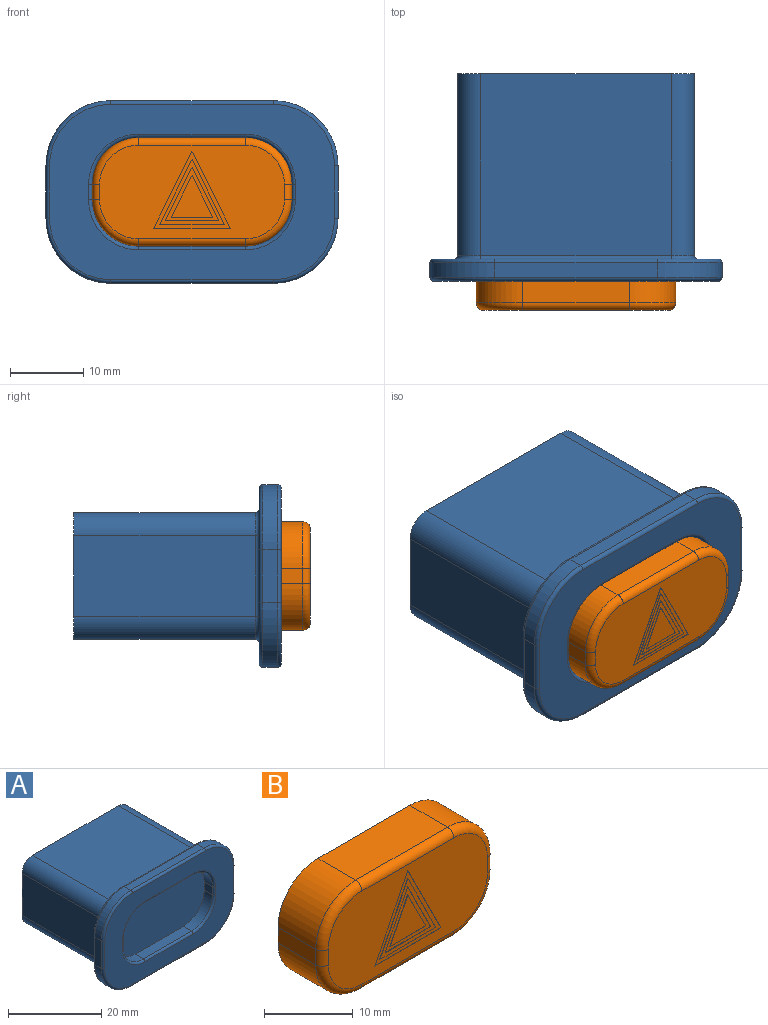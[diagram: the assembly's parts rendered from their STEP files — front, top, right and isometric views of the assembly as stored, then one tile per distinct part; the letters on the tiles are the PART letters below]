
ASSEMBLY  parts=2 mates=1
PART A: 60 faces, bbox 41.5x28.4x26.5 mm
  f0: plane 22.22x2mm, normal (0,0,1), area 44.4mm2, adj f1,f7,f47,f55
  f1: cylinder r=8.89mm len=8.89mm, axis (0,1,0), area 27.9mm2, adj f0,f2,f45,f53
  f2: plane 7.22x2mm, normal (-1,0,0), area 14.4mm2, adj f1,f3,f44,f52
  f3: cylinder r=8.89mm len=8.89mm, axis (0,1,0), area 27.9mm2, adj f2,f4,f46,f54
  f4: plane 22.22x2mm, normal (0,0,-1), area 44.4mm2, adj f3,f5,f48,f56
  f5: cylinder r=8.89mm len=8.89mm, axis (0,1,0), area 27.9mm2, adj f4,f6,f50,f58
  f6: plane 7.22x2mm, normal (1,0,0), area 14.4mm2, adj f5,f7,f51,f59
  f7: cylinder r=8.89mm len=8.89mm, axis (0,1,0), area 27.9mm2, adj f0,f6,f49,f57
  f8: plane 39x24mm, normal (0,-1,0), area 467.6mm2, adj f28,f29,f30,f31,f32,f33,f34,f35
  f9: plane 39x24mm, normal (0,1,0), area 273.6mm2, adj f36,f37,f38,f39,f40,f41,f42,f43
  f10: plane 24.9x11.03mm, normal (1,0,0), area 274.6mm2, adj f11,f17,f18,f40
  f11: cylinder r=3.17mm len=24.9mm, axis (0,-1,0), area 124.2mm2, adj f10,f12,f18,f38
  f12: plane 26.03x24.9mm, normal (0,0,-1), area 648.1mm2, adj f11,f13,f18,f36
  f13: cylinder r=3.17mm len=24.9mm, axis (0,-1,0), area 124.2mm2, adj f12,f14,f18,f37
  f14: plane 24.9x11.03mm, normal (-1,0,0), area 274.6mm2, adj f13,f15,f18,f39
  f15: cylinder r=3.17mm len=24.9mm, axis (0,-1,0), area 124.2mm2, adj f14,f16,f18,f41
  f16: plane 26.03x24.9mm, normal (0,0,1), area 648.1mm2, adj f15,f17,f18,f43
  f17: cylinder r=3.17mm len=24.9mm, axis (0,-1,0), area 124.2mm2, adj f10,f16,f18,f42
  f18: plane 32.38x17.38mm, normal (0,1,0), area 554.1mm2, adj f10,f11,f12,f13,f14,f15,f16,f17
  f19: plane 2.5x2.14mm, normal (1,0,0), area 5.4mm2, adj f20,f26,f27,f32
  f20: cylinder r=6.35mm len=6.35mm, axis (0,-1,0), area 24.9mm2, adj f19,f21,f27,f30
  f21: plane 14.6x2.5mm, normal (0,0,1), area 36.5mm2, adj f20,f22,f27,f28
  f22: cylinder r=6.35mm len=6.35mm, axis (0,-1,0), area 24.9mm2, adj f21,f23,f27,f29
  f23: plane 2.5x2.14mm, normal (-1,0,0), area 5.4mm2, adj f22,f24,f27,f31
  f24: cylinder r=6.35mm len=6.35mm, axis (0,-1,0), area 24.9mm2, adj f23,f25,f27,f33
  f25: plane 14.6x2.5mm, normal (0,0,-1), area 36.5mm2, adj f24,f26,f27,f35
  f26: cylinder r=6.35mm len=6.35mm, axis (0,-1,0), area 24.9mm2, adj f19,f25,f27,f34
  f27: plane 27.3x14.84mm, normal (0,-1,0), area 370.5mm2, adj f19,f20,f21,f22,f23,f24,f25,f26
  f28: cylinder r=0.5mm len=14.6mm, axis (-1,0,0), area 11.5mm2, adj f8,f21,f29,f30
  f29: torus R=6.85mm, axis (0,-1,0), area 8.1mm2, adj f8,f22,f28,f31
  f30: torus R=6.85mm, axis (0,-1,0), area 8.1mm2, adj f8,f20,f28,f32
  f31: cylinder r=0.5mm len=2.14mm, axis (0,0,-1), area 1.7mm2, adj f8,f23,f29,f33
  f32: cylinder r=0.5mm len=2.14mm, axis (0,0,1), area 1.7mm2, adj f8,f19,f30,f34
  f33: torus R=6.85mm, axis (0,-1,0), area 8.1mm2, adj f8,f24,f31,f35
  f34: torus R=6.85mm, axis (0,-1,0), area 8.1mm2, adj f8,f26,f32,f35
  f35: cylinder r=0.5mm len=14.6mm, axis (1,0,0), area 11.5mm2, adj f8,f25,f33,f34
  f36: cylinder r=0.5mm len=26.03mm, axis (1,0,0), area 20.4mm2, adj f9,f12,f37,f38
  f37: torus R=3.67mm, axis (0,-1,0), area 4.1mm2, adj f9,f13,f36,f39
  f38: torus R=3.67mm, axis (0,-1,0), area 4.1mm2, adj f9,f11,f36,f40
  f39: cylinder r=0.5mm len=11.03mm, axis (0,0,-1), area 8.7mm2, adj f9,f14,f37,f41
  f40: cylinder r=0.5mm len=11.03mm, axis (0,0,1), area 8.7mm2, adj f9,f10,f38,f42
  f41: torus R=3.67mm, axis (0,-1,0), area 4.1mm2, adj f9,f15,f39,f43
  f42: torus R=3.67mm, axis (0,-1,0), area 4.1mm2, adj f9,f17,f40,f43
  f43: cylinder r=0.5mm len=26.03mm, axis (-1,0,0), area 20.4mm2, adj f9,f16,f41,f42
  f44: cylinder r=0.5mm len=7.22mm, axis (0,0,-1), area 5.7mm2, adj f2,f9,f45,f46
  f45: torus R=8.39mm, axis (0,-1,0), area 10.7mm2, adj f1,f9,f44,f47
  f46: torus R=8.39mm, axis (0,-1,0), area 10.7mm2, adj f3,f9,f44,f48
  f47: cylinder r=0.5mm len=22.22mm, axis (-1,0,0), area 17.5mm2, adj f0,f9,f45,f49
  f48: cylinder r=0.5mm len=22.22mm, axis (1,0,0), area 17.5mm2, adj f4,f9,f46,f50
  f49: torus R=8.39mm, axis (0,-1,0), area 10.7mm2, adj f7,f9,f47,f51
  f50: torus R=8.39mm, axis (0,-1,0), area 10.7mm2, adj f5,f9,f48,f51
  f51: cylinder r=0.5mm len=7.22mm, axis (0,0,1), area 5.7mm2, adj f6,f9,f49,f50
  f52: cylinder r=0.5mm len=7.22mm, axis (0,0,1), area 5.7mm2, adj f2,f8,f53,f54
  f53: torus R=8.39mm, axis (0,-1,0), area 10.7mm2, adj f1,f8,f52,f55
  f54: torus R=8.39mm, axis (0,-1,0), area 10.7mm2, adj f3,f8,f52,f56
  f55: cylinder r=0.5mm len=22.22mm, axis (1,0,0), area 17.5mm2, adj f0,f8,f53,f57
  f56: cylinder r=0.5mm len=22.22mm, axis (-1,0,0), area 17.5mm2, adj f4,f8,f54,f58
  f57: torus R=8.39mm, axis (0,-1,0), area 10.7mm2, adj f7,f8,f55,f59
  f58: torus R=8.39mm, axis (0,-1,0), area 10.7mm2, adj f5,f8,f56,f59
  f59: cylinder r=0.5mm len=7.22mm, axis (0,0,-1), area 5.7mm2, adj f6,f8,f57,f58
PART B: 34 faces, bbox 28.3x7x15.9 mm
  f0: plane 25.3x12.84mm, normal (0,-1,0), area 245.1mm2, adj f10,f11,f12,f13,f14,f15,f16,f17
  f1: plane 6x2.14mm, normal (-1,0,0), area 12.8mm2, adj f2,f8,f9,f14
  f2: cylinder r=6.35mm len=6.35mm, axis (0,1,0), area 59.8mm2, adj f1,f3,f9,f12
  f3: plane 14.6x6mm, normal (0,0,-1), area 87.6mm2, adj f2,f4,f9,f10
  f4: cylinder r=6.35mm len=6.35mm, axis (0,1,0), area 59.8mm2, adj f3,f5,f9,f11
  f5: plane 6x2.14mm, normal (1,0,0), area 12.8mm2, adj f4,f6,f9,f13
  f6: cylinder r=6.35mm len=6.35mm, axis (0,1,0), area 59.8mm2, adj f5,f7,f9,f15
  f7: plane 14.6x6mm, normal (0,0,1), area 87.6mm2, adj f6,f8,f9,f17
  f8: cylinder r=6.35mm len=6.35mm, axis (0,1,0), area 59.8mm2, adj f1,f7,f9,f16
  f9: plane 27.3x14.84mm, normal (0,1,0), area 370.5mm2, adj f1,f2,f3,f4,f5,f6,f7,f8
  f10: cylinder r=1mm len=14.6mm, axis (-1,0,0), area 22.9mm2, adj f0,f3,f11,f12
  f11: torus R=5.35mm, axis (0,-1,0), area 14.8mm2, adj f0,f4,f10,f13
  f12: torus R=5.35mm, axis (0,-1,0), area 14.8mm2, adj f0,f2,f10,f14
  f13: cylinder r=1mm len=2.14mm, axis (0,0,-1), area 3.4mm2, adj f0,f5,f11,f15
  f14: cylinder r=1mm len=2.14mm, axis (0,0,1), area 3.4mm2, adj f0,f1,f12,f16
  f15: torus R=5.35mm, axis (0,-1,0), area 14.8mm2, adj f0,f6,f13,f17
  f16: torus R=5.35mm, axis (0,-1,0), area 14.8mm2, adj f0,f8,f14,f17
  f17: cylinder r=1mm len=14.6mm, axis (1,0,0), area 22.9mm2, adj f0,f7,f15,f16
  f18: plane 10.51x5.25mm, normal (0.89,0,-0.45), area 0.6mm2, adj f0,f19,f23,f24
  f19: plane 10.51x0.05mm, normal (0,0,1), area 0.5mm2, adj f0,f18,f23,f24
  f20: plane 8.89x0.05mm, normal (0,0,-1), area 0.4mm2, adj f21,f22,f24,f25
  f21: plane 8.89x4.45mm, normal (-0.89,0,0.45), area 0.5mm2, adj f20,f22,f24,f25
  f22: plane 8.89x4.45mm, normal (0.89,0,0.45), area 0.5mm2, adj f20,f21,f24,f25
  f23: plane 10.51x5.25mm, normal (-0.89,0,-0.45), area 0.6mm2, adj f0,f18,f19,f24
  f24: plane 10.51x10.51mm, normal (0,-1,0), area 15.7mm2, adj f18,f19,f20,f21,f22,f23
  f25: plane 8.89x8.89mm, normal (0,-1,0), area 13.1mm2, adj f20,f21,f22,f28,f29,f30
  f26: plane 5.65x2.83mm, normal (-0.89,0,0.45), area 0.3mm2, adj f27,f31,f32,f33
  f27: plane 5.65x2.83mm, normal (0.89,0,0.45), area 0.3mm2, adj f26,f31,f32,f33
  f28: plane 7.27x3.64mm, normal (-0.89,0,-0.45), area 0.4mm2, adj f25,f29,f30,f32
  f29: plane 7.27x3.64mm, normal (0.89,0,-0.45), area 0.4mm2, adj f25,f28,f30,f32
  f30: plane 7.27x0.05mm, normal (0,0,1), area 0.4mm2, adj f25,f28,f29,f32
  f31: plane 5.65x0.05mm, normal (0,0,-1), area 0.3mm2, adj f26,f27,f32,f33
  f32: plane 7.27x7.27mm, normal (0,-1,0), area 10.5mm2, adj f26,f27,f28,f29,f30,f31
  f33: plane 5.65x5.65mm, normal (0,-1,0), area 16mm2, adj f26,f27,f31
PLACE A at identity fixed
PLACE B at identity
MATE fastened B.f9 <-> A.f27  axis (0,1,0) through (0,0,0)mm
